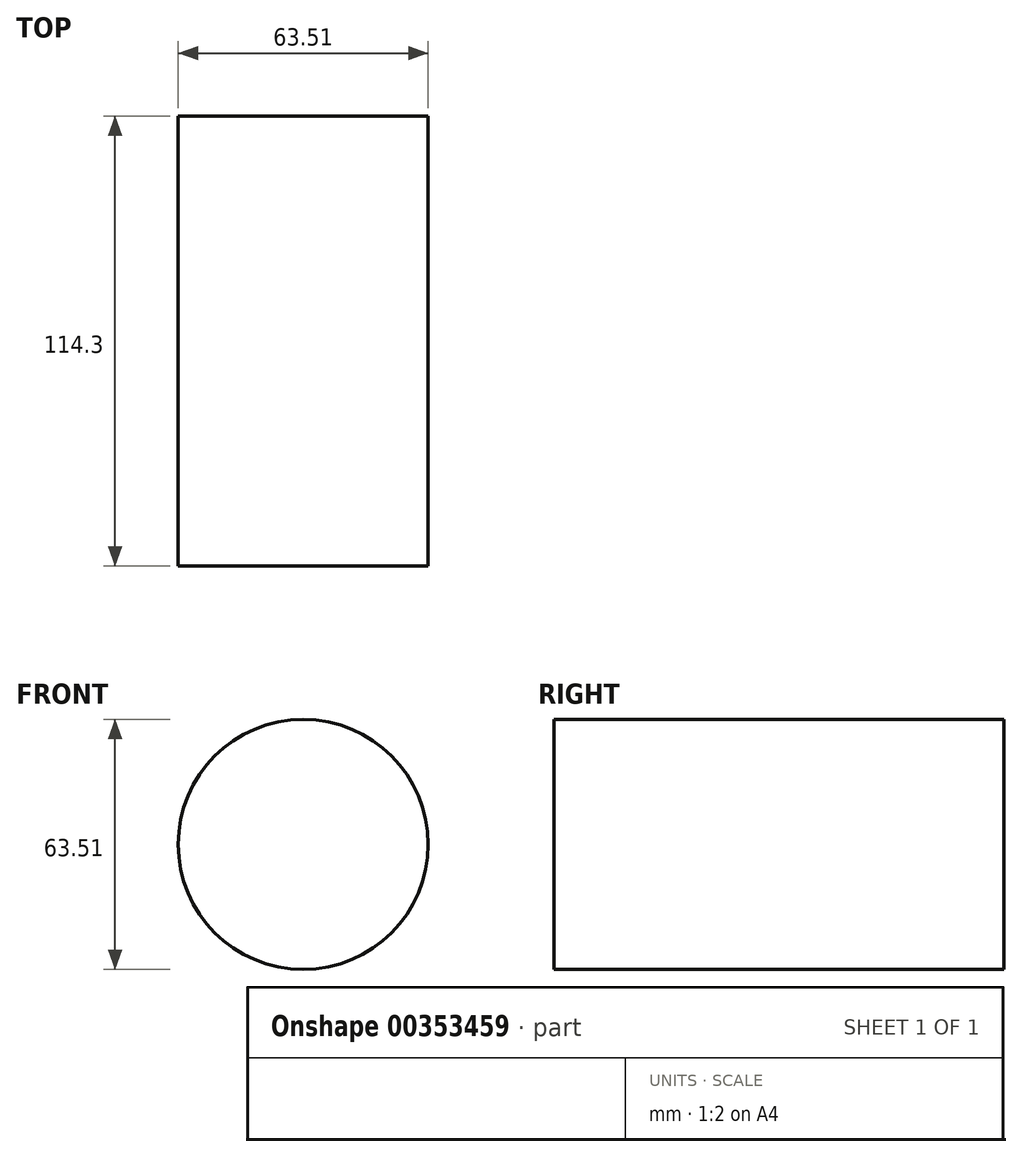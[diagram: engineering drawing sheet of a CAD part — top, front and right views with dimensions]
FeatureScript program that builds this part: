
annotation { "Feature Type Name" : "Feature", "Feature Type Description" : "" }
export const myFeature = defineFeature(function(context is Context, id is Id, definition is map)
    precondition{}
    {
        {
            var Q0;
            Q0=qCreatedBy(makeId("Front.planeOp"),FACE);
            var sketch = newSketch(context, id + "F0", { "sketchPlane" : qUnion([Q0])});
            skCircle(sketch, "E0", {"center": v(-59.9, 53.48) * mm, "radius": 31.76 * mm});
            skSolve(sketch);
        }
        {
            var Q0;
            Q0 = qSketchRegion(id + "F0", true);
            extrude(context, id + "F1", {"entities" : qUnion([Q0]), "depth" : 114.3 * mm});
        }
    });
